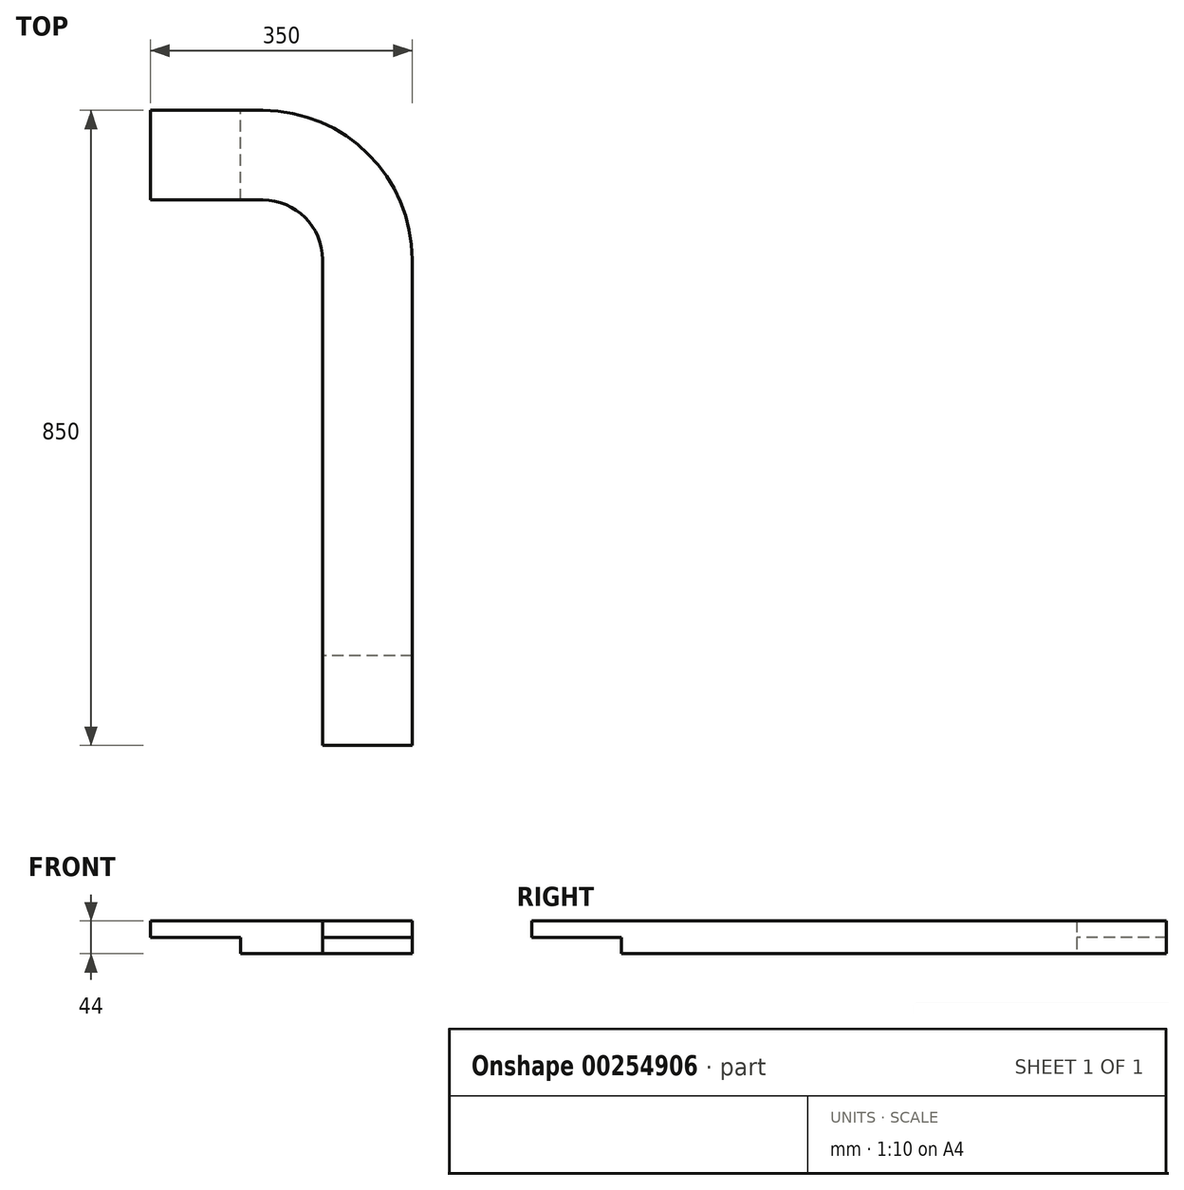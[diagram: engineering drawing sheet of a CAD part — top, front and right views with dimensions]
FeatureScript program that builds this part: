
annotation { "Feature Type Name" : "Feature", "Feature Type Description" : "" }
export const myFeature = defineFeature(function(context is Context, id is Id, definition is map)
    precondition{}
    {
        {
            var Q0;
            Q0=qCreatedBy(makeId("Top.planeOp"),FACE);
            var sketch = newSketch(context, id + "F0", { "sketchPlane" : qUnion([Q0])});
            skLineSegment(sketch, "E0.bottom", {"start": v(0, 0) * mm, "end": v(-120, 0) * mm});
            skLineSegment(sketch, "E0.left", {"start": v(0, 0) * mm, "end": v(0, 650) * mm});
            skLineSegment(sketch, "E0.right", {"start": v(-120, 0) * mm, "end": v(-120, 650) * mm});
            skLineSegment(sketch, "E1", {"start": v(-200, 850) * mm, "end": v(-350, 850) * mm});
            skLineSegment(sketch, "E2", {"start": v(-350, 850) * mm, "end": v(-350, 730) * mm});
            skLineSegment(sketch, "E3", {"start": v(-350, 730) * mm, "end": v(-200, 730) * mm});
            skPoint(sketch, "E4.visualSharp", {"position": v(0, 850) * mm});
            skArc(sketch, "E4.filletArc", {"start": v(0, 650) * mm, "mid": v(-58.58, 791.42) * mm, "end": v(-200, 850) * mm});
            skPoint(sketch, "E5.visualSharp", {"position": v(-120, 730) * mm});
            skArc(sketch, "E5.filletArc", {"start": v(-120, 650) * mm, "mid": v(-143.43, 706.57) * mm, "end": v(-200, 730) * mm});
            skSolve(sketch);
        }
        {
            var Q0;
            Q0=makeQuery(id+"F0.imprint","IMPRINT",FACE,{"disambiguationData":[TD([[makeQuery(id+"F0.imprint","IMPRINT",EDGE,{"derivedFrom":sQuery(id+"F0.wireOp",EDGE,"E0.bottom")}),-1.0]])]});
            extrude(context, id + "F1", {"entities" : qUnion([Q0]), "depth" : 44 * mm});
        }
        {
            var Q0;
            Q0=makeQuery(id+"F1.opExtrude","CAP_FACE",FACE,{"disambiguationData":[OSD([sQuery(id+"F0.wireOp",EDGE,"E0.bottom"),sQuery(id+"F0.wireOp",EDGE,"E0.left"),sQuery(id+"F0.wireOp",EDGE,"E0.right"),sQuery(id+"F0.wireOp",EDGE,"E1"),sQuery(id+"F0.wireOp",EDGE,"E2"),sQuery(id+"F0.wireOp",EDGE,"E3"),sQuery(id+"F0.wireOp",EDGE,"E4.filletArc"),sQuery(id+"F0.wireOp",EDGE,"E5.filletArc")])],"isStart":true});
            var sketch = newSketch(context, id + "F2", { "sketchPlane" : qUnion([Q0])});
            skLineSegment(sketch, "E6.bottom", {"start": v(0, 0) * mm, "end": v(-120, 0) * mm});
            skLineSegment(sketch, "E6.top", {"start": v(0, -120) * mm, "end": v(-120, -120) * mm});
            skLineSegment(sketch, "E6.left", {"start": v(0, 0) * mm, "end": v(0, -120) * mm});
            skLineSegment(sketch, "E6.right", {"start": v(-120, 0) * mm, "end": v(-120, -120) * mm});
            skSolve(sketch);
        }
        {
            var Q0;
            Q0=makeQuery(id+"F2.imprint","IMPRINT",FACE,{"disambiguationData":[TD([[makeQuery(id+"F2.imprint","IMPRINT",EDGE,{"derivedFrom":sQuery(id+"F2.wireOp",EDGE,"E6.bottom")}),1.0]])]});
            extrude(context, id + "F3", {"entities" : qUnion([Q0]), "operationType" : NewBodyOperationType.REMOVE, "oppositeDirection" : true, "depth" : 22 * mm});
        }
        {
            var Q0;
            Q0=makeQuery(id+"F1.opExtrude","CAP_FACE",FACE,{"disambiguationData":[OSD([sQuery(id+"F0.wireOp",EDGE,"E0.bottom"),sQuery(id+"F0.wireOp",EDGE,"E0.left"),sQuery(id+"F0.wireOp",EDGE,"E0.right"),sQuery(id+"F0.wireOp",EDGE,"E1"),sQuery(id+"F0.wireOp",EDGE,"E2"),sQuery(id+"F0.wireOp",EDGE,"E3"),sQuery(id+"F0.wireOp",EDGE,"E4.filletArc"),sQuery(id+"F0.wireOp",EDGE,"E5.filletArc")])],"isStart":true});
            var sketch = newSketch(context, id + "F4", { "sketchPlane" : qUnion([Q0])});
            skLineSegment(sketch, "E7.bottom", {"start": v(-350, -730) * mm, "end": v(-230, -730) * mm});
            skLineSegment(sketch, "E7.top", {"start": v(-350, -850) * mm, "end": v(-230, -850) * mm});
            skLineSegment(sketch, "E7.left", {"start": v(-350, -730) * mm, "end": v(-350, -850) * mm});
            skLineSegment(sketch, "E7.right", {"start": v(-230, -730) * mm, "end": v(-230, -850) * mm});
            skSolve(sketch);
        }
        {
            var Q0;
            Q0=makeQuery(id+"F4.imprint","IMPRINT",FACE,{"disambiguationData":[TD([[makeQuery(id+"F4.imprint","IMPRINT",EDGE,{"derivedFrom":sQuery(id+"F4.wireOp",EDGE,"E7.bottom")}),-1.0]])]});
            extrude(context, id + "F5", {"entities" : qUnion([Q0]), "operationType" : NewBodyOperationType.REMOVE, "oppositeDirection" : true, "depth" : 22 * mm});
        }
    });
